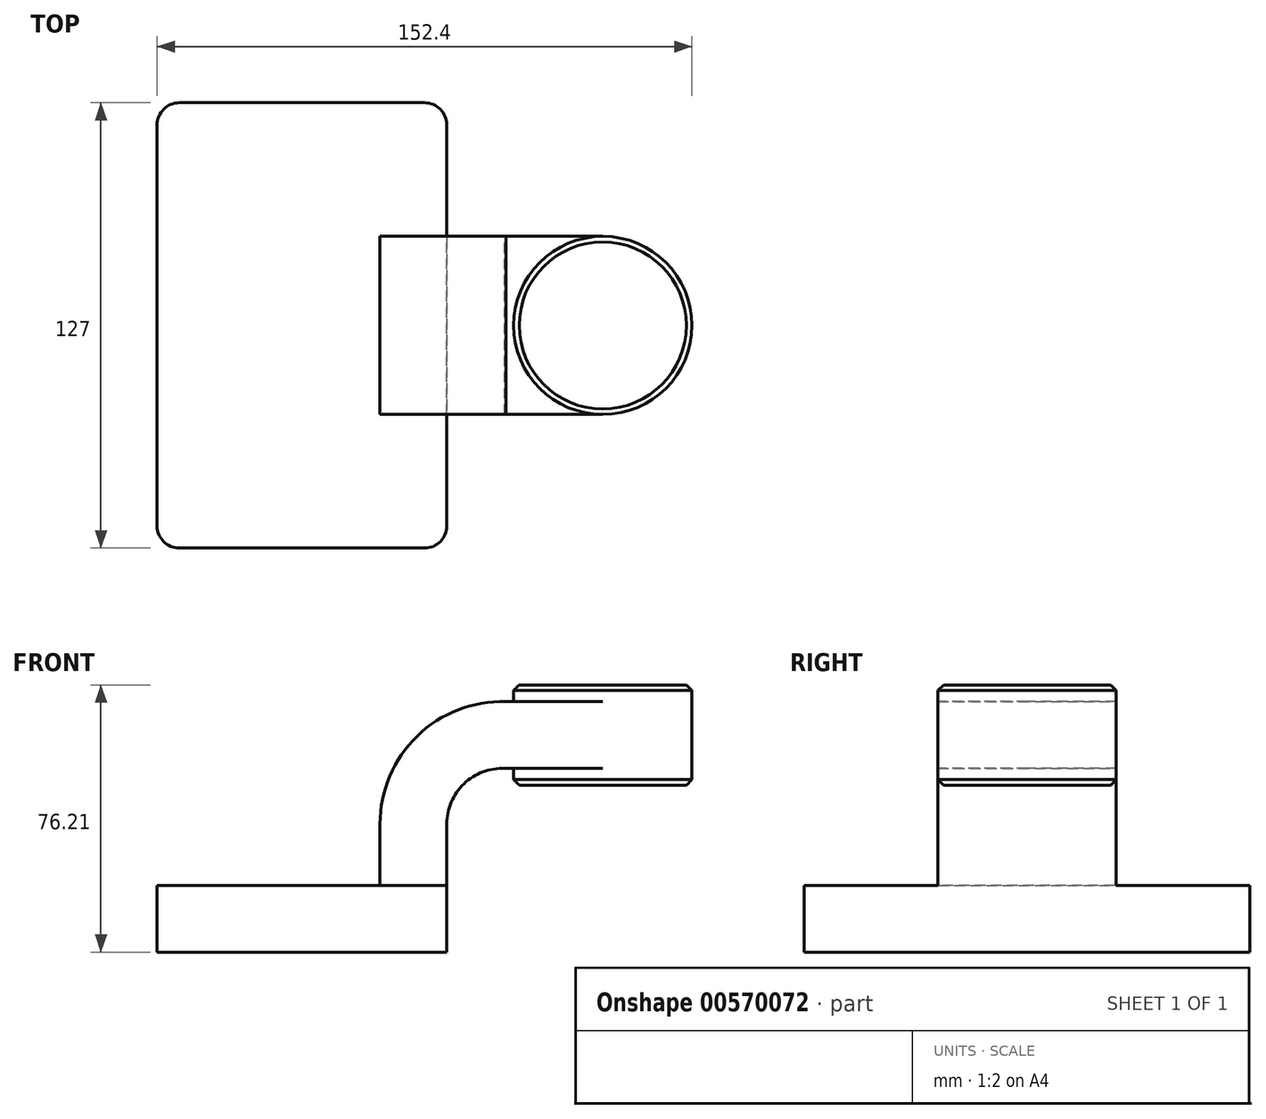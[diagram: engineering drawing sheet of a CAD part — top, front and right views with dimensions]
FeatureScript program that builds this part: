
annotation { "Feature Type Name" : "Feature", "Feature Type Description" : "" }
export const myFeature = defineFeature(function(context is Context, id is Id, definition is map)
    precondition{}
    {
        {
            var Q0;
            Q0=qCreatedBy(makeId("Front.planeOp"),FACE);
            var sketch = newSketch(context, id + "F0", { "sketchPlane" : qUnion([Q0])});
            skLineSegment(sketch, "E0.bottom", {"start": v(41.28, -9.52) * mm, "end": v(-41.28, -9.52) * mm});
            skLineSegment(sketch, "E0.top", {"start": v(41.27, 9.53) * mm, "end": v(-41.28, 9.53) * mm});
            skLineSegment(sketch, "E0.left", {"start": v(41.28, -9.52) * mm, "end": v(41.28, 9.53) * mm});
            skLineSegment(sketch, "E0.right", {"start": v(-41.28, -9.52) * mm, "end": v(-41.28, 9.53) * mm});
            skPoint(sketch, "E0.middle", {"position": v(0, 0) * mm});
            skLineSegment(sketch, "E1.bottom", {"start": v(111.13, 38.1) * mm, "end": v(60.33, 38.1) * mm});
            skLineSegment(sketch, "E1.top", {"start": v(111.13, 66.68) * mm, "end": v(60.33, 66.68) * mm});
            skLineSegment(sketch, "E1.left", {"start": v(111.13, 38.1) * mm, "end": v(111.13, 66.68) * mm});
            skLineSegment(sketch, "E1.right", {"start": v(60.33, 38.1) * mm, "end": v(60.33, 66.68) * mm});
            skPoint(sketch, "E1.middle", {"position": v(85.73, 52.39) * mm});
            skLineSegment(sketch, "E2", {"start": v(41.27, 9.53) * mm, "end": v(41.27, 27) * mm});
            skArc(sketch, "E3", {"start": v(41.27, 27) * mm, "mid": v(46.17, 38.46) * mm, "end": v(57.83, 42.86) * mm});
            skLineSegment(sketch, "E4", {"start": v(57.83, 42.86) * mm, "end": v(85.72, 42.86) * mm});
            skLineSegment(sketch, "E5.0", {"start": v(58.15, 61.91) * mm, "end": v(85.72, 61.91) * mm});
            skArc(sketch, "E5.1", {"start": v(22.23, 27) * mm, "mid": v(32.81, 52.05) * mm, "end": v(58.15, 61.91) * mm});
            skLineSegment(sketch, "E5.2", {"start": v(22.22, 9.53) * mm, "end": v(22.22, 27) * mm});
            skFitSpline(sketch, "E6", {"points": [v(-41.28, 9.53) * mm, v(58.15, 61.91) * mm], "startDerivative": vector(-2.54, 76.43) * mm, "endDerivative": vector(136.3, -17.75) * mm});
            skLineSegment(sketch, "E7", {"start": v(85.72, 66.68) * mm, "end": v(85.72, 38.1) * mm});
            skSolve(sketch);
        }
        {
            var Q0;
            Q0=makeQuery(id+"F0.imprint","IMPRINT",FACE,{"disambiguationData":[TD([[makeQuery(id+"F0.imprint","IMPRINT",EDGE,{"derivedFrom":sQuery(id+"F0.wireOp",EDGE,"E0.bottom")}),-1.0]])]});
            extrude(context, id + "F1", {"entities" : qUnion([Q0]), "endBound" : BoundingType.SYMMETRIC, "oppositeDirection" : true, "depth" : 127 * mm, "offsetDistance" : 25.4 * mm});
        }
        {
            var Q0;
            {var subQ1=sQuery(id+"F0.wireOp",EDGE,"E2");Q0=makeQuery(id+"F0.imprint","IMPRINT",FACE,{"disambiguationData":[TD([[makeQuery(id+"F0.imprint","IMPRINT",EDGE,{"derivedFrom":subQ1}),1.0]])]});}
            var Q1;
            {var subQ0=sQuery(id+"F0.wireOp",EDGE,"E4");var subQ1=sQuery(id+"F0.wireOp",EDGE,"E1.right");var subQ2=makeQuery(id+"F0.imprint","INTERSECT",VERTEX,{"derivedFrom":[subQ1,subQ0]});Q1=makeQuery(id+"F0.imprint","IMPRINT",FACE,{"disambiguationData":[TD([[makeQuery(id+"F0.imprint","IMPRINT",EDGE,{"disambiguationData":[TD([[subQ2,-1.0]])],"derivedFrom":subQ1}),-1.0]])]});}
            extrude(context, id + "F2", {"entities" : qUnion([Q0, Q1]), "operationType" : NewBodyOperationType.ADD, "endBound" : BoundingType.SYMMETRIC, "depth" : 50.8 * mm, "offsetDistance" : 25.4 * mm});
        }
        {
            var Q0;
            Q0=makeQuery(id+"F0.imprint","IMPRINT",FACE,{"disambiguationData":[TD([[makeQuery(id+"F0.imprint","IMPRINT",EDGE,{"derivedFrom":sQuery(id+"F0.wireOp",EDGE,"E5.1")}),1.0]])]});
            extrude(context, id + "F3", {"entities" : qUnion([Q0]), "operationType" : NewBodyOperationType.ADD, "endBound" : BoundingType.SYMMETRIC, "depth" : 15.88 * mm, "offsetDistance" : 25.4 * mm});
        }
        {
            var Q0;
            {var subQ0=sQuery(id+"F0.wireOp",EDGE,"E1.left");Q0=makeQuery(id+"F0.imprint","IMPRINT",FACE,{"disambiguationData":[TD([[makeQuery(id+"F0.imprint","IMPRINT",EDGE,{"derivedFrom":subQ0}),1.0]])]});}
            var Q1;
            Q1=sQuery(id+"F0.wireOp",EDGE,"E7");
            revolve(context, id + "F4", {"operationType" : NewBodyOperationType.ADD, "entities" : qUnion([Q0]), "axis" : qUnion([Q1]), "revolveType" : RevolveType.FULL});
        }
        {
            var Q0;
            Q0=makeQuery(id+"F1.opExtrude","CAP_EDGE",EDGE,{"disambiguationData":[OSD([sQuery(id+"F0.wireOp",EDGE,"E0.left")])],"isStart":true});
            var Q1;
            Q1=makeQuery(id+"F1.opExtrude","CAP_EDGE",EDGE,{"disambiguationData":[OSD([sQuery(id+"F0.wireOp",EDGE,"E0.left")])],"isStart":false});
            var Q2;
            Q2=makeQuery(id+"F1.opExtrude","CAP_EDGE",EDGE,{"disambiguationData":[OSD([sQuery(id+"F0.wireOp",EDGE,"E0.right")])],"isStart":true});
            var Q3;
            Q3=makeQuery(id+"F1.opExtrude","CAP_EDGE",EDGE,{"disambiguationData":[OSD([sQuery(id+"F0.wireOp",EDGE,"E0.right")])],"isStart":false});
            fillet(context, id + "F5", {"entities" : qUnion([Q0, Q1, Q2, Q3]), "radius" : 6.35 * mm, "tangentPropagation" : true, "allowEdgeOverflow" : false});
        }
        {
            var Q0;
            Q0=makeQuery(id+"F4.opRevolve","SWEPT_EDGE",EDGE,{"disambiguationData":[OSD([sQuery(id+"F0.wireOp",EDGE,"E1.top"),sQuery(id+"F0.wireOp",EDGE,"E1.left")])]});
            var Q1;
            Q1=makeQuery(id+"F4.opRevolve","SWEPT_EDGE",EDGE,{"disambiguationData":[OSD([sQuery(id+"F0.wireOp",EDGE,"E1.bottom"),sQuery(id+"F0.wireOp",EDGE,"E1.left")])]});
            chamfer(context, id + "F6", {"entities" : qUnion([Q0, Q1]), "width" : 1.59 * mm, "tangentPropagation" : true});
        }
    });
